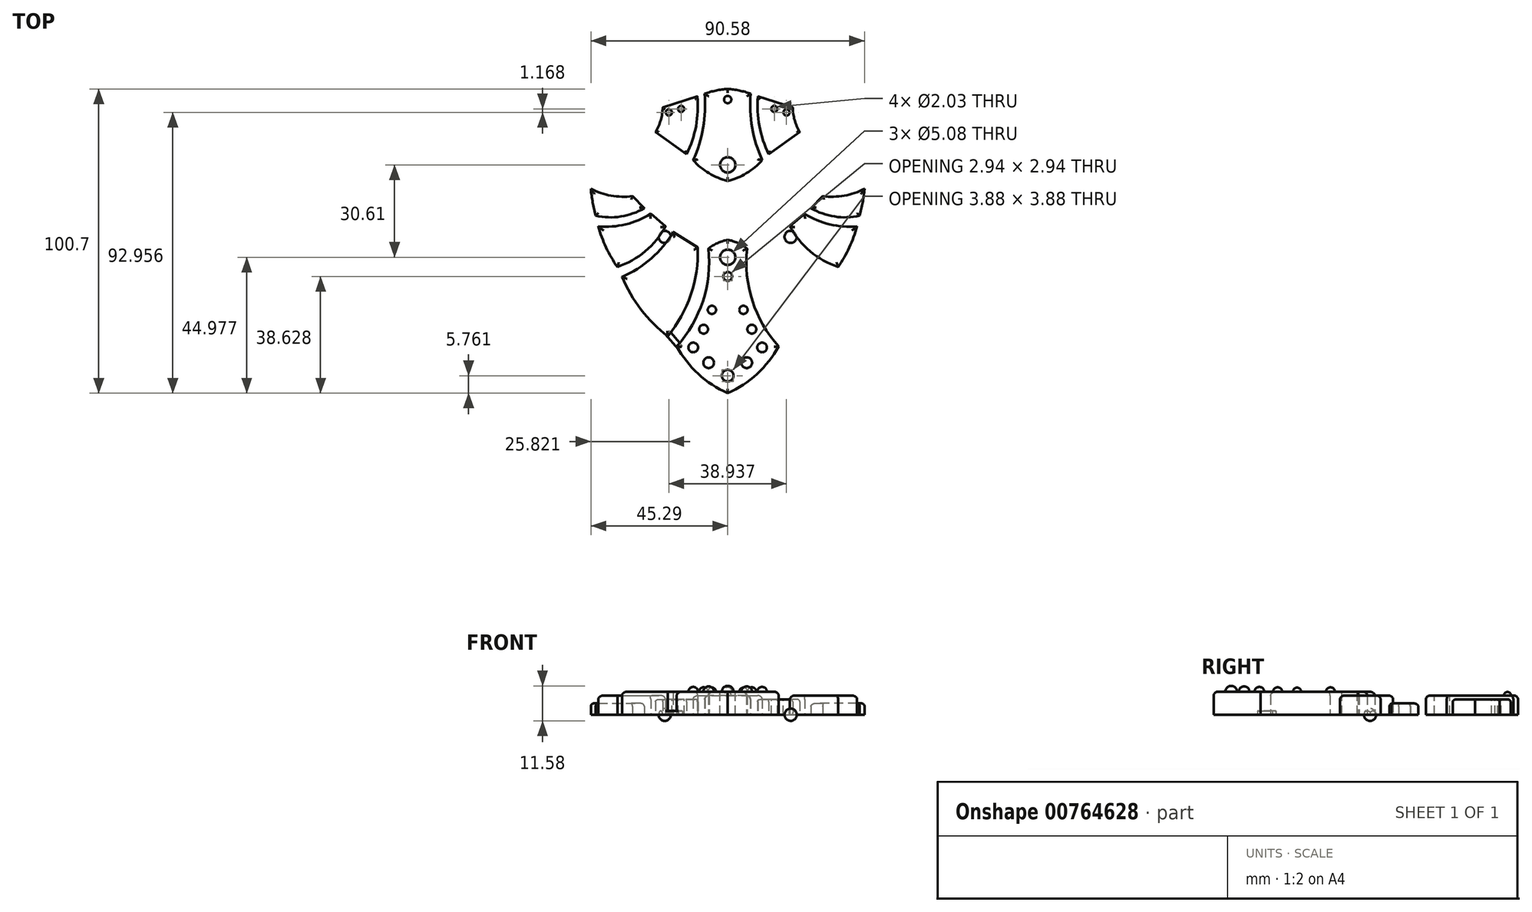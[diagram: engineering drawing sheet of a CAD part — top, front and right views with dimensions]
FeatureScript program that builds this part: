
annotation { "Feature Type Name" : "Feature", "Feature Type Description" : "" }
export const myFeature = defineFeature(function(context is Context, id is Id, definition is map)
    precondition{}
    {
        {
            var Q0;
            Q0=qCreatedBy(makeId("Top.planeOp"),FACE);
            var sketch = newSketch(context, id + "F0", { "sketchPlane" : qUnion([Q0])});
            skArc(sketch, "E0", {"start": v(0, 35.33) * mm, "mid": v(-3.38, 34.2) * mm, "end": v(-6.4, 32.34) * mm});
            skArc(sketch, "E1", {"start": v(-16.87, 0) * mm, "mid": v(-8.18, 15.05) * mm, "end": v(-6.4, 32.34) * mm});
            skArc(sketch, "E2", {"start": v(-16.87, 0) * mm, "mid": v(-9.71, -9.13) * mm, "end": v(0, -15.47) * mm});
            skArc(sketch, "E3.MirrorCS", {"start": v(16.87, 0) * mm, "mid": v(8.18, 15.05) * mm, "end": v(6.4, 32.34) * mm});
            skArc(sketch, "E4.MirrorCS", {"start": v(0, 35.33) * mm, "mid": v(3.38, 34.2) * mm, "end": v(6.4, 32.34) * mm});
            skArc(sketch, "E5.MirrorCS", {"start": v(16.87, 0) * mm, "mid": v(9.71, -9.13) * mm, "end": v(0, -15.47) * mm});
            skSolve(sketch);
        }
        {
            var Q0;
            Q0=makeQuery(id+"F0.imprint","IMPRINT",FACE,{"disambiguationData":[TD([[makeQuery(id+"F0.imprint","IMPRINT",EDGE,{"derivedFrom":sQuery(id+"F0.wireOp",EDGE,"E0")}),1.0]])]});
            extrude(context, id + "F1", {"entities" : qUnion([Q0]), "depth" : 7.62 * mm, "offsetDistance" : 25.4 * mm});
        }
        {
            var Q0;
            Q0=makeQuery(id+"F1.opExtrude","CAP_EDGE",EDGE,{"disambiguationData":[OSD([sQuery(id+"F0.wireOp",EDGE,"E5.MirrorCS")])],"isStart":false});
            var Q1;
            Q1=makeQuery(id+"F1.opExtrude","CAP_FACE",FACE,{"disambiguationData":[OSD([sQuery(id+"F0.wireOp",EDGE,"E0"),sQuery(id+"F0.wireOp",EDGE,"E1"),sQuery(id+"F0.wireOp",EDGE,"E2"),sQuery(id+"F0.wireOp",EDGE,"E3.MirrorCS"),sQuery(id+"F0.wireOp",EDGE,"E4.MirrorCS"),sQuery(id+"F0.wireOp",EDGE,"E5.MirrorCS")])],"isStart":false});
            fillet(context, id + "F2", {"entities" : qUnion([Q0, Q1]), "radius" : 1.27 * mm, "tangentPropagation" : true, "allowEdgeOverflow" : false});
        }
        {
            var Q0;
            Q0=makeQuery(id+"F1.opExtrude","CAP_FACE",FACE,{"disambiguationData":[OSD([sQuery(id+"F0.wireOp",EDGE,"E0"),sQuery(id+"F0.wireOp",EDGE,"E1"),sQuery(id+"F0.wireOp",EDGE,"E2"),sQuery(id+"F0.wireOp",EDGE,"E3.MirrorCS"),sQuery(id+"F0.wireOp",EDGE,"E4.MirrorCS"),sQuery(id+"F0.wireOp",EDGE,"E5.MirrorCS")])],"isStart":false});
            var sketch = newSketch(context, id + "F3", { "sketchPlane" : qUnion([Q0])});
            skCircle(sketch, "E6", {"center": v(0, 29.5) * mm, "radius": 1.8 * mm});
            skSolve(sketch);
        }
        {
            var Q0;
            Q0=sQuery(id+"F3.wireOp",VERTEX,"E6.center");
            var Q1;
            Q1=makeQuery(id+"F1.opExtrude","SWEPT_BODY",BODY,{"disambiguationData":[OSD([sQuery(id+"F0.wireOp",EDGE,"E0"),sQuery(id+"F0.wireOp",EDGE,"E1"),sQuery(id+"F0.wireOp",EDGE,"E2"),sQuery(id+"F0.wireOp",EDGE,"E3.MirrorCS"),sQuery(id+"F0.wireOp",EDGE,"E4.MirrorCS"),sQuery(id+"F0.wireOp",EDGE,"E5.MirrorCS")])]});
            hole(context, id + "F4", {"style" : HoleStyle.SIMPLE, "endStyle" : HoleEndStyle.THROUGH, "holeDiameter" : 5.08 * mm, "majorDiameter" : 6.35 * mm, "isTappedThrough" : true, "tappedDepth" : 12.7 * mm, "tapClearance" : 3, "locations" : qUnion([Q0]), "scope" : qUnion([Q1])});
        }
        {
            var Q0;
            Q0=makeQuery(id+"F1.opExtrude","CAP_FACE",FACE,{"disambiguationData":[OSD([sQuery(id+"F0.wireOp",EDGE,"E0"),sQuery(id+"F0.wireOp",EDGE,"E1"),sQuery(id+"F0.wireOp",EDGE,"E2"),sQuery(id+"F0.wireOp",EDGE,"E3.MirrorCS"),sQuery(id+"F0.wireOp",EDGE,"E4.MirrorCS"),sQuery(id+"F0.wireOp",EDGE,"E5.MirrorCS")])],"isStart":false});
            var sketch = newSketch(context, id + "F5", { "sketchPlane" : qUnion([Q0])});
            skArc(sketch, "E7", {"start": v(0, -11.65) * mm, "mid": v(1.94, -9.7) * mm, "end": v(0, -7.77) * mm});
            skLineSegment(sketch, "E8", {"start": v(0, -7.77) * mm, "end": v(0, -11.65) * mm});
            skSolve(sketch);
        }
        {
            var Q0;
            Q0=makeQuery(id+"F5.imprint","IMPRINT",FACE,{"disambiguationData":[TD([[makeQuery(id+"F5.imprint","IMPRINT",EDGE,{"derivedFrom":sQuery(id+"F5.wireOp",EDGE,"E7")}),1.0]])]});
            var Q1;
            Q1=sQuery(id+"F5.wireOp",EDGE,"E7");
            var Q2;
            Q2=sQuery(id+"F5.wireOp",EDGE,"E8");
            revolve(context, id + "F6", {"operationType" : NewBodyOperationType.ADD, "surfaceOperationType" : NewSurfaceOperationType.ADD, "entities" : qUnion([Q0]), "surfaceEntities" : qUnion([Q1]), "axis" : qUnion([Q2]), "revolveType" : RevolveType.ONE_DIRECTION, "angle" : 180 * degree});
        }
        {
            var Q0;
            Q0=qCreatedBy(makeId("Top.planeOp"),FACE);
            var sketch = newSketch(context, id + "F7", { "sketchPlane" : qUnion([Q0])});
            skArc(sketch, "E9", {"start": v(0, 85.23) * mm, "mid": v(-3.88, 84.74) * mm, "end": v(-7.63, 83.67) * mm});
            skArc(sketch, "E10", {"start": v(-11.43, 61.67) * mm, "mid": v(-8.1, 72.42) * mm, "end": v(-7.63, 83.67) * mm});
            skArc(sketch, "E11", {"start": v(-11.43, 61.67) * mm, "mid": v(-6.23, 57.37) * mm, "end": v(0, 54.75) * mm});
            skArc(sketch, "E12.MirrorCS", {"start": v(11.43, 61.67) * mm, "mid": v(6.23, 57.37) * mm, "end": v(0, 54.75) * mm});
            skArc(sketch, "E13.MirrorCS", {"start": v(0, 85.23) * mm, "mid": v(3.88, 84.74) * mm, "end": v(7.63, 83.67) * mm});
            skArc(sketch, "E14.MirrorCS", {"start": v(11.43, 61.67) * mm, "mid": v(8.1, 72.42) * mm, "end": v(7.63, 83.67) * mm});
            skSolve(sketch);
        }
        {
            var Q0;
            Q0=qSketchRegion(id+"F7",true);
            extrude(context, id + "F8", {"entities" : qUnion([Q0]), "depth" : 6.35 * mm, "offsetDistance" : 25.4 * mm});
        }
        {
            var Q0;
            Q0=makeQuery(id+"F8.opExtrude","CAP_EDGE",EDGE,{"disambiguationData":[OSD([sQuery(id+"F7.wireOp",EDGE,"E14.MirrorCS")])],"isStart":false});
            var Q1;
            Q1=makeQuery(id+"F8.opExtrude","CAP_EDGE",EDGE,{"disambiguationData":[OSD([sQuery(id+"F7.wireOp",EDGE,"E10")])],"isStart":false});
            var Q2;
            Q2=makeQuery(id+"F8.opExtrude","CAP_FACE",FACE,{"disambiguationData":[OSD([sQuery(id+"F7.wireOp",EDGE,"E9"),sQuery(id+"F7.wireOp",EDGE,"E10"),sQuery(id+"F7.wireOp",EDGE,"E11"),sQuery(id+"F7.wireOp",EDGE,"E12.MirrorCS"),sQuery(id+"F7.wireOp",EDGE,"E13.MirrorCS"),sQuery(id+"F7.wireOp",EDGE,"E14.MirrorCS")])],"isStart":false});
            fillet(context, id + "F9", {"entities" : qUnion([Q0, Q1, Q2]), "radius" : 1.27 * mm, "tangentPropagation" : true, "allowEdgeOverflow" : false});
        }
        {
            var Q0;
            Q0=makeQuery(id+"F8.opExtrude","CAP_FACE",FACE,{"disambiguationData":[OSD([sQuery(id+"F7.wireOp",EDGE,"E9"),sQuery(id+"F7.wireOp",EDGE,"E10"),sQuery(id+"F7.wireOp",EDGE,"E11"),sQuery(id+"F7.wireOp",EDGE,"E12.MirrorCS"),sQuery(id+"F7.wireOp",EDGE,"E13.MirrorCS"),sQuery(id+"F7.wireOp",EDGE,"E14.MirrorCS")])],"isStart":false});
            var sketch = newSketch(context, id + "F10", { "sketchPlane" : qUnion([Q0])});
            skCircle(sketch, "E15", {"center": v(0, 60.12) * mm, "radius": 1.7 * mm});
            skSolve(sketch);
        }
        {
            var Q0;
            Q0=sQuery(id+"F10.wireOp",VERTEX,"E15.center");
            var Q1;
            Q1=makeQuery(id+"F8.opExtrude","SWEPT_BODY",BODY,{"disambiguationData":[OSD([sQuery(id+"F7.wireOp",EDGE,"E9"),sQuery(id+"F7.wireOp",EDGE,"E10"),sQuery(id+"F7.wireOp",EDGE,"E11"),sQuery(id+"F7.wireOp",EDGE,"E12.MirrorCS"),sQuery(id+"F7.wireOp",EDGE,"E13.MirrorCS"),sQuery(id+"F7.wireOp",EDGE,"E14.MirrorCS")])]});
            hole(context, id + "F11", {"style" : HoleStyle.SIMPLE, "endStyle" : HoleEndStyle.THROUGH, "holeDiameter" : 5.08 * mm, "majorDiameter" : 6.35 * mm, "isTappedThrough" : true, "tappedDepth" : 12.7 * mm, "tapClearance" : 3, "locations" : qUnion([Q0]), "scope" : qUnion([Q1])});
        }
        {
            var Q0;
            Q0=qCreatedBy(makeId("Top.planeOp"),FACE);
            var sketch = newSketch(context, id + "F12", { "sketchPlane" : qUnion([Q0])});
            skLineSegment(sketch, "E16", {"start": v(-10, 82.76) * mm, "end": v(-21.52, 79.1) * mm});
            skArc(sketch, "E17", {"start": v(-23.89, 70.98) * mm, "mid": v(-22.16, 74.88) * mm, "end": v(-21.52, 79.1) * mm});
            skLineSegment(sketch, "E18", {"start": v(-23.89, 70.98) * mm, "end": v(-13.58, 63.66) * mm});
            skArc(sketch, "E19", {"start": v(-13.58, 63.66) * mm, "mid": v(-10.49, 72.97) * mm, "end": v(-10, 82.76) * mm});
            skSolve(sketch);
        }
        {
            var Q0;
            Q0=makeQuery(id+"F12.imprint","IMPRINT",FACE,{"disambiguationData":[TD([[makeQuery(id+"F12.imprint","IMPRINT",EDGE,{"derivedFrom":sQuery(id+"F12.wireOp",EDGE,"E16")}),1.0]])]});
            extrude(context, id + "F13", {"entities" : qUnion([Q0]), "depth" : 5.08 * mm, "offsetDistance" : 25.4 * mm});
        }
        {
            var Q0;
            Q0=makeQuery(id+"F13.opExtrude","CAP_FACE",FACE,{"disambiguationData":[OSD([sQuery(id+"F12.wireOp",EDGE,"E16"),sQuery(id+"F12.wireOp",EDGE,"E17"),sQuery(id+"F12.wireOp",EDGE,"E18"),sQuery(id+"F12.wireOp",EDGE,"E19")])],"isStart":false});
            fillet(context, id + "F14", {"entities" : qUnion([Q0]), "radius" : 0.76 * mm, "tangentPropagation" : true, "allowEdgeOverflow" : false});
        }
        {
            var Q0;
            Q0=qCreatedBy(makeId("Top.planeOp"),FACE);
            var sketch = newSketch(context, id + "F15", { "sketchPlane" : qUnion([Q0])});
            skLineSegment(sketch, "E20", {"start": v(-9.9, 32.72) * mm, "end": v(-18, 37.86) * mm});
            skArc(sketch, "E21", {"start": v(-34.99, 23.02) * mm, "mid": v(-25.3, 29.08) * mm, "end": v(-18, 37.86) * mm});
            skArc(sketch, "E22", {"start": v(-34.99, 23.02) * mm, "mid": v(-28.71, 12.18) * mm, "end": v(-19.8, 3.37) * mm});
            skArc(sketch, "E23", {"start": v(-19.8, 3.37) * mm, "mid": v(-12.2, 17.15) * mm, "end": v(-9.9, 32.72) * mm});
            skSolve(sketch);
        }
        {
            var Q0;
            Q0=makeQuery(id+"F15.imprint","IMPRINT",FACE,{"disambiguationData":[TD([[makeQuery(id+"F15.imprint","IMPRINT",EDGE,{"derivedFrom":sQuery(id+"F15.wireOp",EDGE,"E20")}),1.0]])]});
            extrude(context, id + "F16", {"entities" : qUnion([Q0]), "depth" : 7.62 * mm, "offsetDistance" : 25.4 * mm});
        }
        {
            var Q0;
            Q0=makeQuery(id+"F16.opExtrude","CAP_FACE",FACE,{"disambiguationData":[OSD([sQuery(id+"F15.wireOp",EDGE,"E20"),sQuery(id+"F15.wireOp",EDGE,"E21"),sQuery(id+"F15.wireOp",EDGE,"E22"),sQuery(id+"F15.wireOp",EDGE,"E23")])],"isStart":false});
            fillet(context, id + "F17", {"entities" : qUnion([Q0]), "radius" : 1.27 * mm, "tangentPropagation" : true, "allowEdgeOverflow" : false});
        }
        {
            var Q0;
            Q0=qCreatedBy(makeId("Top.planeOp"),FACE);
            var sketch = newSketch(context, id + "F18", { "sketchPlane" : qUnion([Q0])});
            skLineSegment(sketch, "E24", {"start": v(-20.6, 39.74) * mm, "end": v(-25.48, 43.9) * mm});
            skArc(sketch, "E25", {"start": v(-36.53, 26.3) * mm, "mid": v(-27.28, 31.5) * mm, "end": v(-20.6, 39.74) * mm});
            skArc(sketch, "E26", {"start": v(-42.83, 39.74) * mm, "mid": v(-40.25, 32.76) * mm, "end": v(-36.53, 26.3) * mm});
            skArc(sketch, "E27", {"start": v(-42.83, 39.74) * mm, "mid": v(-33.81, 40.39) * mm, "end": v(-25.48, 43.9) * mm});
            skSolve(sketch);
        }
        {
            var Q0;
            Q0=makeQuery(id+"F18.imprint","IMPRINT",FACE,{"disambiguationData":[TD([[makeQuery(id+"F18.imprint","IMPRINT",EDGE,{"derivedFrom":sQuery(id+"F18.wireOp",EDGE,"E24")}),1.0]])]});
            extrude(context, id + "F19", {"entities" : qUnion([Q0]), "depth" : 6.35 * mm, "offsetDistance" : 25.4 * mm});
        }
        {
            var Q0;
            Q0=makeQuery(id+"F19.opExtrude","CAP_FACE",FACE,{"disambiguationData":[OSD([sQuery(id+"F18.wireOp",EDGE,"E24"),sQuery(id+"F18.wireOp",EDGE,"E25"),sQuery(id+"F18.wireOp",EDGE,"E26"),sQuery(id+"F18.wireOp",EDGE,"E27")])],"isStart":false});
            fillet(context, id + "F20", {"entities" : qUnion([Q0]), "radius" : 1.27 * mm, "tangentPropagation" : true, "allowEdgeOverflow" : false});
        }
        {
            var Q0;
            Q0=qCreatedBy(makeId("Top.planeOp"),FACE);
            var sketch = newSketch(context, id + "F21", { "sketchPlane" : qUnion([Q0])});
            skLineSegment(sketch, "E28", {"start": v(-27.58, 45.78) * mm, "end": v(-31.53, 49.73) * mm});
            skArc(sketch, "E29", {"start": v(-43.67, 43.28) * mm, "mid": v(-35.38, 43) * mm, "end": v(-27.58, 45.78) * mm});
            skArc(sketch, "E30", {"start": v(-45.3, 52.16) * mm, "mid": v(-44.67, 47.69) * mm, "end": v(-43.67, 43.28) * mm});
            skArc(sketch, "E31", {"start": v(-45.3, 52.16) * mm, "mid": v(-38.6, 49.92) * mm, "end": v(-31.53, 49.73) * mm});
            skSolve(sketch);
        }
        {
            var Q0;
            Q0=makeQuery(id+"F21.imprint","IMPRINT",FACE,{"disambiguationData":[TD([[makeQuery(id+"F21.imprint","IMPRINT",EDGE,{"derivedFrom":sQuery(id+"F21.wireOp",EDGE,"E28")}),1.0]])]});
            extrude(context, id + "F22", {"entities" : qUnion([Q0]), "depth" : 3.8 * mm, "offsetDistance" : 25.4 * mm});
        }
        {
            var Q0;
            Q0=makeQuery(id+"F22.opExtrude","CAP_FACE",FACE,{"disambiguationData":[OSD([sQuery(id+"F21.wireOp",EDGE,"E28"),sQuery(id+"F21.wireOp",EDGE,"E29"),sQuery(id+"F21.wireOp",EDGE,"E30"),sQuery(id+"F21.wireOp",EDGE,"E31")])],"isStart":false});
            fillet(context, id + "F23", {"entities" : qUnion([Q0]), "radius" : 1.02 * mm, "tangentPropagation" : true, "allowEdgeOverflow" : false});
        }
        {
            var Q0;
            Q0=makeQuery(id+"F13.opExtrude","CAP_FACE",FACE,{"disambiguationData":[OSD([sQuery(id+"F12.wireOp",EDGE,"E16"),sQuery(id+"F12.wireOp",EDGE,"E17"),sQuery(id+"F12.wireOp",EDGE,"E18"),sQuery(id+"F12.wireOp",EDGE,"E19")])],"isStart":false});
            var sketch = newSketch(context, id + "F24", { "sketchPlane" : qUnion([Q0])});
            skCircle(sketch, "E32", {"center": v(-19.47, 77.49) * mm, "radius": 1.02 * mm});
            skSolve(sketch);
        }
        {
            var Q0;
            Q0=sQuery(id+"F24.wireOp",VERTEX,"E32.center");
            var Q1;
            Q1=makeQuery(id+"F13.opExtrude","SWEPT_BODY",BODY,{"disambiguationData":[OSD([sQuery(id+"F12.wireOp",EDGE,"E16"),sQuery(id+"F12.wireOp",EDGE,"E17"),sQuery(id+"F12.wireOp",EDGE,"E18"),sQuery(id+"F12.wireOp",EDGE,"E19")])]});
            hole(context, id + "F25", {"style" : HoleStyle.SIMPLE, "endStyle" : HoleEndStyle.THROUGH, "holeDiameter" : 2.03 * mm, "majorDiameter" : 6.35 * mm, "isTappedThrough" : true, "tappedDepth" : 12.7 * mm, "tapClearance" : 3, "locations" : qUnion([Q0]), "scope" : qUnion([Q1])});
        }
        {
            var Q0;
            Q0=makeQuery(id+"F13.opExtrude","CAP_FACE",FACE,{"disambiguationData":[OSD([sQuery(id+"F12.wireOp",EDGE,"E16"),sQuery(id+"F12.wireOp",EDGE,"E17"),sQuery(id+"F12.wireOp",EDGE,"E18"),sQuery(id+"F12.wireOp",EDGE,"E19")])],"isStart":false});
            var sketch = newSketch(context, id + "F26", { "sketchPlane" : qUnion([Q0])});
            skCircle(sketch, "E33", {"center": v(-15.42, 78.65) * mm, "radius": 1.01 * mm});
            skSolve(sketch);
        }
        {
            var Q0;
            Q0=sQuery(id+"F26.wireOp",VERTEX,"E33.center");
            var Q1;
            Q1=makeQuery(id+"F13.opExtrude","SWEPT_BODY",BODY,{"disambiguationData":[OSD([sQuery(id+"F12.wireOp",EDGE,"E16"),sQuery(id+"F12.wireOp",EDGE,"E17"),sQuery(id+"F12.wireOp",EDGE,"E18"),sQuery(id+"F12.wireOp",EDGE,"E19")])]});
            hole(context, id + "F27", {"style" : HoleStyle.SIMPLE, "endStyle" : HoleEndStyle.THROUGH, "holeDiameter" : 2.03 * mm, "majorDiameter" : 6.35 * mm, "isTappedThrough" : true, "tappedDepth" : 12.7 * mm, "tapClearance" : 3, "locations" : qUnion([Q0]), "scope" : qUnion([Q1])});
        }
        {
            var Q0;
            Q0=makeQuery(id+"F8.opExtrude","CAP_FACE",FACE,{"disambiguationData":[OSD([sQuery(id+"F7.wireOp",EDGE,"E9"),sQuery(id+"F7.wireOp",EDGE,"E10"),sQuery(id+"F7.wireOp",EDGE,"E11"),sQuery(id+"F7.wireOp",EDGE,"E12.MirrorCS"),sQuery(id+"F7.wireOp",EDGE,"E13.MirrorCS"),sQuery(id+"F7.wireOp",EDGE,"E14.MirrorCS")])],"isStart":false});
            var sketch = newSketch(context, id + "F28", { "sketchPlane" : qUnion([Q0])});
            skArc(sketch, "E34", {"start": v(0, 82.96) * mm, "mid": v(-1.21, 81.75) * mm, "end": v(0, 80.54) * mm});
            skLineSegment(sketch, "E35", {"start": v(0, 82.96) * mm, "end": v(0, 80.54) * mm});
            skSolve(sketch);
        }
        {
            var Q0;
            Q0=makeQuery(id+"F28.imprint","IMPRINT",FACE,{"disambiguationData":[TD([[makeQuery(id+"F28.imprint","IMPRINT",EDGE,{"derivedFrom":sQuery(id+"F28.wireOp",EDGE,"E34")}),1.0]])]});
            var Q1;
            Q1=sQuery(id+"F28.wireOp",EDGE,"E34");
            var Q2;
            Q2=sQuery(id+"F28.wireOp",EDGE,"E35");
            revolve(context, id + "F29", {"operationType" : NewBodyOperationType.ADD, "surfaceOperationType" : NewSurfaceOperationType.NEW, "entities" : qUnion([Q0]), "surfaceEntities" : qUnion([Q1]), "axis" : qUnion([Q2]), "revolveType" : RevolveType.FULL});
        }
        {
            var Q0;
            Q0=makeQuery(id+"F1.opExtrude","CAP_FACE",FACE,{"disambiguationData":[OSD([sQuery(id+"F0.wireOp",EDGE,"E0"),sQuery(id+"F0.wireOp",EDGE,"E1"),sQuery(id+"F0.wireOp",EDGE,"E2"),sQuery(id+"F0.wireOp",EDGE,"E3.MirrorCS"),sQuery(id+"F0.wireOp",EDGE,"E4.MirrorCS"),sQuery(id+"F0.wireOp",EDGE,"E5.MirrorCS")])],"isStart":false});
            var sketch = newSketch(context, id + "F30", { "sketchPlane" : qUnion([Q0])});
            skArc(sketch, "E36", {"start": v(-11.39, 1.23) * mm, "mid": v(-12.98, -0.37) * mm, "end": v(-11.39, -1.97) * mm});
            skLineSegment(sketch, "E37", {"start": v(-11.39, 1.23) * mm, "end": v(-11.39, -1.97) * mm});
            skSolve(sketch);
        }
        {
            var Q0;
            Q0=makeQuery(id+"F30.imprint","IMPRINT",FACE,{"disambiguationData":[TD([[makeQuery(id+"F30.imprint","IMPRINT",EDGE,{"derivedFrom":sQuery(id+"F30.wireOp",EDGE,"E36")}),1.0]])]});
            var Q1;
            Q1=sQuery(id+"F30.wireOp",EDGE,"E36");
            var Q2;
            Q2=sQuery(id+"F30.wireOp",EDGE,"E37");
            revolve(context, id + "F31", {"operationType" : NewBodyOperationType.ADD, "surfaceOperationType" : NewSurfaceOperationType.ADD, "entities" : qUnion([Q0]), "surfaceEntities" : qUnion([Q1]), "axis" : qUnion([Q2]), "revolveType" : RevolveType.FULL});
        }
        {
            var Q0;
            Q0=qCreatedBy(makeId("Top.planeOp"),FACE);
            var sketch = newSketch(context, id + "F32", { "sketchPlane" : qUnion([Q0])});
            skArc(sketch, "E38", {"start": v(-8.2, 27.38) * mm, "mid": v(-5.99, 29.58) * mm, "end": v(-8.2, 31.79) * mm});
            skLineSegment(sketch, "E39", {"start": v(-8.2, 27.38) * mm, "end": v(-8.2, 31.79) * mm});
            skSolve(sketch);
        }
        {
            var Q0;
            Q0=sQuery(id+"F32.wireOp",EDGE,"E38");
            var Q1;
            Q1=sQuery(id+"F32.wireOp",EDGE,"E39");
            revolve(context, id + "F33", {"bodyType" : ToolBodyType.SURFACE, "surfaceOperationType" : NewSurfaceOperationType.NEW, "surfaceEntities" : qUnion([Q0]), "axis" : qUnion([Q1]), "revolveType" : RevolveType.FULL});
        }
        {
            var Q0;
            Q0=qCreatedBy(makeId("Top.planeOp"),FACE);
            var sketch = newSketch(context, id + "F34", { "sketchPlane" : qUnion([Q0])});
            skArc(sketch, "E40", {"start": v(-20.84, 34.25) * mm, "mid": v(-18.82, 36.27) * mm, "end": v(-20.84, 38.3) * mm});
            skLineSegment(sketch, "E41", {"start": v(-20.84, 34.25) * mm, "end": v(-20.84, 38.3) * mm});
            skSolve(sketch);
        }
        {
            var Q0;
            Q0=qSketchRegion(id+"F34",true);
            var Q1;
            Q1=sQuery(id+"F34.wireOp",EDGE,"E41");
            revolve(context, id + "F35", {"surfaceOperationType" : NewSurfaceOperationType.NEW, "entities" : qUnion([Q0]), "axis" : qUnion([Q1]), "revolveType" : RevolveType.FULL});
        }
        {
            var Q0;
            Q0=qCreatedBy(makeId("Top.planeOp"),FACE);
            var sketch = newSketch(context, id + "F36", { "sketchPlane" : qUnion([Q0])});
            skArc(sketch, "E42", {"start": v(-29.07, 41.32) * mm, "mid": v(-27.22, 43.18) * mm, "end": v(-29.07, 45.03) * mm});
            skLineSegment(sketch, "E43", {"start": v(-29.07, 41.32) * mm, "end": v(-29.07, 45.03) * mm});
            skSolve(sketch);
        }
        {
            var Q0;
            Q0=sQuery(id+"F36.wireOp",EDGE,"E42");
            var Q1;
            Q1=sQuery(id+"F36.wireOp",EDGE,"E43");
            revolve(context, id + "F37", {"bodyType" : ToolBodyType.SURFACE, "surfaceOperationType" : NewSurfaceOperationType.NEW, "surfaceEntities" : qUnion([Q0]), "axis" : qUnion([Q1]), "revolveType" : RevolveType.FULL});
        }
        {
            var Q0;
            Q0=makeQuery(id+"F1.opExtrude","CAP_FACE",FACE,{"disambiguationData":[OSD([sQuery(id+"F0.wireOp",EDGE,"E0"),sQuery(id+"F0.wireOp",EDGE,"E1"),sQuery(id+"F0.wireOp",EDGE,"E2"),sQuery(id+"F0.wireOp",EDGE,"E3.MirrorCS"),sQuery(id+"F0.wireOp",EDGE,"E4.MirrorCS"),sQuery(id+"F0.wireOp",EDGE,"E5.MirrorCS")])],"isStart":false});
            var sketch = newSketch(context, id + "F38", { "sketchPlane" : qUnion([Q0])});
            skArc(sketch, "E44", {"start": v(-6.3, -7.2) * mm, "mid": v(-4.53, -5.42) * mm, "end": v(-6.3, -3.65) * mm});
            skLineSegment(sketch, "E45", {"start": v(-6.3, -3.65) * mm, "end": v(-6.3, -7.2) * mm});
            skSolve(sketch);
        }
        {
            var Q0;
            Q0=makeQuery(id+"F38.imprint","IMPRINT",FACE,{"disambiguationData":[TD([[makeQuery(id+"F38.imprint","IMPRINT",EDGE,{"derivedFrom":sQuery(id+"F38.wireOp",EDGE,"E44")}),1.0]])]});
            var Q1;
            Q1=sQuery(id+"F38.wireOp",EDGE,"E44");
            var Q2;
            Q2=sQuery(id+"F38.wireOp",EDGE,"E45");
            revolve(context, id + "F39", {"operationType" : NewBodyOperationType.ADD, "surfaceOperationType" : NewSurfaceOperationType.NEW, "entities" : qUnion([Q0]), "surfaceEntities" : qUnion([Q1]), "axis" : qUnion([Q2]), "revolveType" : RevolveType.FULL});
        }
        {
            var Q0;
            Q0=makeQuery(id+"F1.opExtrude","CAP_FACE",FACE,{"disambiguationData":[OSD([sQuery(id+"F0.wireOp",EDGE,"E0"),sQuery(id+"F0.wireOp",EDGE,"E1"),sQuery(id+"F0.wireOp",EDGE,"E2"),sQuery(id+"F0.wireOp",EDGE,"E3.MirrorCS"),sQuery(id+"F0.wireOp",EDGE,"E4.MirrorCS"),sQuery(id+"F0.wireOp",EDGE,"E5.MirrorCS")])],"isStart":false});
            var sketch = newSketch(context, id + "F40", { "sketchPlane" : qUnion([Q0])});
            skArc(sketch, "E46", {"start": v(-7.98, 4.2) * mm, "mid": v(-6.5, 5.68) * mm, "end": v(-7.98, 7.16) * mm});
            skLineSegment(sketch, "E47", {"start": v(-7.98, 7.16) * mm, "end": v(-7.98, 4.2) * mm});
            skSolve(sketch);
        }
        {
            var Q0;
            Q0=makeQuery(id+"F40.imprint","IMPRINT",FACE,{"disambiguationData":[TD([[makeQuery(id+"F40.imprint","IMPRINT",EDGE,{"derivedFrom":sQuery(id+"F40.wireOp",EDGE,"E46")}),1.0]])]});
            var Q1;
            Q1=sQuery(id+"F40.wireOp",EDGE,"E46");
            var Q2;
            Q2=sQuery(id+"F40.wireOp",EDGE,"E47");
            revolve(context, id + "F41", {"operationType" : NewBodyOperationType.ADD, "surfaceOperationType" : NewSurfaceOperationType.NEW, "entities" : qUnion([Q0]), "surfaceEntities" : qUnion([Q1]), "axis" : qUnion([Q2]), "revolveType" : RevolveType.FULL});
        }
        {
            var Q0;
            Q0=qCreatedBy(makeId("Top.planeOp"),FACE);
            var sketch = newSketch(context, id + "F42", { "sketchPlane" : qUnion([Q0])});
            skLineSegment(sketch, "E48", {"start": v(-20.58, 3.98) * mm, "end": v(-16.29, -0.95) * mm});
            skLineSegment(sketch, "E49", {"start": v(-16.29, -0.95) * mm, "end": v(-15.04, 0.14) * mm});
            skLineSegment(sketch, "E50", {"start": v(-15.04, 0.14) * mm, "end": v(-19.4, 5.14) * mm});
            skLineSegment(sketch, "E51", {"start": v(-19.4, 5.14) * mm, "end": v(-20.58, 3.98) * mm});
            skSolve(sketch);
        }
        {
            var Q0;
            Q0=makeQuery(id+"F42.imprint","IMPRINT",FACE,{"disambiguationData":[TD([[makeQuery(id+"F42.imprint","IMPRINT",EDGE,{"derivedFrom":sQuery(id+"F42.wireOp",EDGE,"E48")}),1.0]])]});
            extrude(context, id + "F43", {"entities" : qUnion([Q0]), "depth" : 1.27 * mm, "offsetDistance" : 25.4 * mm});
        }
        {
            var Q0;
            Q0=makeQuery(id+"F1.opExtrude","CAP_FACE",FACE,{"disambiguationData":[OSD([sQuery(id+"F0.wireOp",EDGE,"E0"),sQuery(id+"F0.wireOp",EDGE,"E1"),sQuery(id+"F0.wireOp",EDGE,"E2"),sQuery(id+"F0.wireOp",EDGE,"E3.MirrorCS"),sQuery(id+"F0.wireOp",EDGE,"E4.MirrorCS"),sQuery(id+"F0.wireOp",EDGE,"E5.MirrorCS")])],"isStart":false});
            var sketch = newSketch(context, id + "F44", { "sketchPlane" : qUnion([Q0])});
            skArc(sketch, "E52", {"start": v(-5.22, 10.73) * mm, "mid": v(-3.85, 12.1) * mm, "end": v(-5.22, 13.46) * mm});
            skLineSegment(sketch, "E53", {"start": v(-5.22, 13.46) * mm, "end": v(-5.22, 10.73) * mm});
            skSolve(sketch);
        }
        {
            var Q0;
            Q0=makeQuery(id+"F44.imprint","IMPRINT",FACE,{"disambiguationData":[TD([[makeQuery(id+"F44.imprint","IMPRINT",EDGE,{"derivedFrom":sQuery(id+"F44.wireOp",EDGE,"E52")}),1.0]])]});
            var Q1;
            Q1=sQuery(id+"F44.wireOp",EDGE,"E52");
            var Q2;
            Q2=sQuery(id+"F44.wireOp",EDGE,"E53");
            revolve(context, id + "F45", {"operationType" : NewBodyOperationType.ADD, "surfaceOperationType" : NewSurfaceOperationType.NEW, "entities" : qUnion([Q0]), "surfaceEntities" : qUnion([Q1]), "axis" : qUnion([Q2]), "revolveType" : RevolveType.FULL});
        }
        {
            var Q0;
            Q0=makeQuery(id+"F1.opExtrude","CAP_FACE",FACE,{"disambiguationData":[OSD([sQuery(id+"F0.wireOp",EDGE,"E0"),sQuery(id+"F0.wireOp",EDGE,"E1"),sQuery(id+"F0.wireOp",EDGE,"E2"),sQuery(id+"F0.wireOp",EDGE,"E3.MirrorCS"),sQuery(id+"F0.wireOp",EDGE,"E4.MirrorCS"),sQuery(id+"F0.wireOp",EDGE,"E5.MirrorCS")])],"isStart":false});
            var sketch = newSketch(context, id + "F46", { "sketchPlane" : qUnion([Q0])});
            skArc(sketch, "E54", {"start": v(-3.58, 17.36) * mm, "mid": v(-2.32, 18.63) * mm, "end": v(-3.58, 19.9) * mm});
            skLineSegment(sketch, "E55", {"start": v(-3.58, 19.9) * mm, "end": v(-3.58, 17.36) * mm});
            skSolve(sketch);
        }
        {
            var Q0;
            Q0=sQuery(id+"F46.wireOp",EDGE,"E54");
            var Q1;
            Q1=sQuery(id+"F46.wireOp",EDGE,"E55");
            revolve(context, id + "F47", {"bodyType" : ToolBodyType.SURFACE, "surfaceOperationType" : NewSurfaceOperationType.NEW, "surfaceEntities" : qUnion([Q0]), "axis" : qUnion([Q1]), "revolveType" : RevolveType.FULL});
        }
        {
            var Q0;
            Q0=makeQuery(id+"F47.opRevolve","SWEPT_BODY",BODY,{"disambiguationData":[OSD([sQuery(id+"F46.wireOp",EDGE,"E54")])]});
            var Q1;
            Q1=qCreatedBy(makeId("Right.planeOp"),FACE);
            mirror(context, id + "F48", {"entities" : qUnion([Q0]), "mirrorPlane" : qUnion([Q1])});
        }
        {
            var Q0;
            Q0=makeQuery(id+"F1.opExtrude","CAP_FACE",FACE,{"disambiguationData":[OSD([sQuery(id+"F0.wireOp",EDGE,"E0"),sQuery(id+"F0.wireOp",EDGE,"E1"),sQuery(id+"F0.wireOp",EDGE,"E2"),sQuery(id+"F0.wireOp",EDGE,"E3.MirrorCS"),sQuery(id+"F0.wireOp",EDGE,"E4.MirrorCS"),sQuery(id+"F0.wireOp",EDGE,"E5.MirrorCS")])],"isStart":false});
            var sketch = newSketch(context, id + "F49", { "sketchPlane" : qUnion([Q0])});
            skArc(sketch, "E56", {"start": v(0, 21.69) * mm, "mid": v(1.47, 23.16) * mm, "end": v(0, 24.63) * mm});
            skLineSegment(sketch, "E57", {"start": v(0, 24.63) * mm, "end": v(0, 21.69) * mm});
            skSolve(sketch);
        }
        {
            var Q0;
            Q0=makeQuery(id+"F49.imprint","IMPRINT",FACE,{"disambiguationData":[TD([[makeQuery(id+"F49.imprint","IMPRINT",EDGE,{"derivedFrom":sQuery(id+"F49.wireOp",EDGE,"E56")}),1.0]])]});
            var Q1;
            Q1=sQuery(id+"F49.wireOp",EDGE,"E56");
            var Q2;
            Q2=sQuery(id+"F49.wireOp",EDGE,"E57");
            revolve(context, id + "F50", {"operationType" : NewBodyOperationType.ADD, "surfaceOperationType" : NewSurfaceOperationType.NEW, "entities" : qUnion([Q0]), "surfaceEntities" : qUnion([Q1]), "axis" : qUnion([Q2]), "revolveType" : RevolveType.FULL});
        }
        {
            var Q0;
            Q0=makeQuery(id+"F8.opExtrude","CAP_FACE",FACE,{"disambiguationData":[OSD([sQuery(id+"F7.wireOp",EDGE,"E9"),sQuery(id+"F7.wireOp",EDGE,"E10"),sQuery(id+"F7.wireOp",EDGE,"E11"),sQuery(id+"F7.wireOp",EDGE,"E12.MirrorCS"),sQuery(id+"F7.wireOp",EDGE,"E13.MirrorCS"),sQuery(id+"F7.wireOp",EDGE,"E14.MirrorCS")])],"isStart":false});
            var sketch = newSketch(context, id + "F51", { "sketchPlane" : qUnion([Q0])});
            skArc(sketch, "E58", {"start": v(-4.05, 80.13) * mm, "mid": v(-2.9, 81.3) * mm, "end": v(-4.05, 82.46) * mm});
            skLineSegment(sketch, "E59", {"start": v(-4.05, 82.46) * mm, "end": v(-4.05, 80.13) * mm});
            skSolve(sketch);
        }
        {
            var Q0;
            Q0=sQuery(id+"F51.wireOp",EDGE,"E58");
            var Q1;
            Q1=sQuery(id+"F51.wireOp",EDGE,"E59");
            revolve(context, id + "F52", {"bodyType" : ToolBodyType.SURFACE, "surfaceOperationType" : NewSurfaceOperationType.NEW, "surfaceEntities" : qUnion([Q0]), "axis" : qUnion([Q1]), "revolveType" : RevolveType.FULL});
        }
        {
            var Q0;
            Q0=makeQuery(id+"F52.opRevolve","SWEPT_BODY",BODY,{"disambiguationData":[OSD([sQuery(id+"F51.wireOp",EDGE,"E58")])]});
            var Q1;
            Q1=qCreatedBy(makeId("Right.planeOp"),FACE);
            mirror(context, id + "F53", {"entities" : qUnion([Q0]), "mirrorPlane" : qUnion([Q1])});
        }
        {
            var Q0;
            Q0=makeQuery(id+"F8.opExtrude","CAP_FACE",FACE,{"disambiguationData":[OSD([sQuery(id+"F7.wireOp",EDGE,"E9"),sQuery(id+"F7.wireOp",EDGE,"E10"),sQuery(id+"F7.wireOp",EDGE,"E11"),sQuery(id+"F7.wireOp",EDGE,"E12.MirrorCS"),sQuery(id+"F7.wireOp",EDGE,"E13.MirrorCS"),sQuery(id+"F7.wireOp",EDGE,"E14.MirrorCS")])],"isStart":false});
            var sketch = newSketch(context, id + "F54", { "sketchPlane" : qUnion([Q0])});
            skArc(sketch, "E60", {"start": v(-6.03, 60.77) * mm, "mid": v(-4.09, 62.72) * mm, "end": v(-6.03, 64.67) * mm});
            skLineSegment(sketch, "E61", {"start": v(-6.03, 64.67) * mm, "end": v(-6.03, 60.77) * mm});
            skSolve(sketch);
        }
        {
            var Q0;
            Q0=sQuery(id+"F54.wireOp",EDGE,"E60");
            var Q1;
            Q1=sQuery(id+"F54.wireOp",EDGE,"E61");
            revolve(context, id + "F55", {"bodyType" : ToolBodyType.SURFACE, "surfaceOperationType" : NewSurfaceOperationType.NEW, "surfaceEntities" : qUnion([Q0]), "axis" : qUnion([Q1]), "revolveType" : RevolveType.FULL});
        }
        {
            var Q0;
            Q0=makeQuery(id+"F55.opRevolve","SWEPT_BODY",BODY,{"disambiguationData":[OSD([sQuery(id+"F54.wireOp",EDGE,"E60")])]});
            var Q1;
            Q1=qCreatedBy(makeId("Right.planeOp"),FACE);
            mirror(context, id + "F56", {"entities" : qUnion([Q0]), "mirrorPlane" : qUnion([Q1])});
        }
        {
            var Q0;
            Q0=qCreatedBy(makeId("Top.planeOp"),FACE);
            var sketch = newSketch(context, id + "F57", { "sketchPlane" : qUnion([Q0])});
            skArc(sketch, "E62", {"start": v(-8.7, 78.7) * mm, "mid": v(-7.1, 80.3) * mm, "end": v(-8.7, 81.93) * mm});
            skLineSegment(sketch, "E63", {"start": v(-8.7, 78.7) * mm, "end": v(-8.7, 81.93) * mm});
            skSolve(sketch);
        }
        {
            var Q0;
            Q0=sQuery(id+"F57.wireOp",EDGE,"E62");
            var Q1;
            Q1=sQuery(id+"F57.wireOp",EDGE,"E63");
            revolve(context, id + "F58", {"bodyType" : ToolBodyType.SURFACE, "surfaceOperationType" : NewSurfaceOperationType.NEW, "surfaceEntities" : qUnion([Q0]), "axis" : qUnion([Q1]), "revolveType" : RevolveType.FULL});
        }
        {
            var Q0;
            Q0=makeQuery(id+"F16.opExtrude","CAP_FACE",FACE,{"disambiguationData":[OSD([sQuery(id+"F15.wireOp",EDGE,"E20"),sQuery(id+"F15.wireOp",EDGE,"E21"),sQuery(id+"F15.wireOp",EDGE,"E22"),sQuery(id+"F15.wireOp",EDGE,"E23")])],"isStart":false});
            var sketch = newSketch(context, id + "F59", { "sketchPlane" : qUnion([Q0])});
            skArc(sketch, "E64", {"start": v(-20.59, 8.42) * mm, "mid": v(-19.03, 9.98) * mm, "end": v(-20.59, 11.54) * mm});
            skLineSegment(sketch, "E65", {"start": v(-20.59, 11.54) * mm, "end": v(-20.59, 8.42) * mm});
            skSolve(sketch);
        }
        {
            var Q0;
            Q0=sQuery(id+"F59.wireOp",EDGE,"E64");
            var Q1;
            Q1=sQuery(id+"F59.wireOp",EDGE,"E65");
            revolve(context, id + "F60", {"bodyType" : ToolBodyType.SURFACE, "surfaceOperationType" : NewSurfaceOperationType.NEW, "surfaceEntities" : qUnion([Q0]), "axis" : qUnion([Q1]), "revolveType" : RevolveType.FULL});
        }
        {
            var Q0;
            Q0=makeQuery(id+"F16.opExtrude","CAP_FACE",FACE,{"disambiguationData":[OSD([sQuery(id+"F15.wireOp",EDGE,"E20"),sQuery(id+"F15.wireOp",EDGE,"E21"),sQuery(id+"F15.wireOp",EDGE,"E22"),sQuery(id+"F15.wireOp",EDGE,"E23")])],"isStart":false});
            var sketch = newSketch(context, id + "F61", { "sketchPlane" : qUnion([Q0])});
            skArc(sketch, "E66", {"start": v(-17.5, 13.56) * mm, "mid": v(-16.15, 14.91) * mm, "end": v(-17.5, 16.26) * mm});
            skLineSegment(sketch, "E67", {"start": v(-17.5, 16.26) * mm, "end": v(-17.5, 13.56) * mm});
            skSolve(sketch);
        }
        {
            var Q0;
            Q0=sQuery(id+"F61.wireOp",EDGE,"E66");
            var Q1;
            Q1=sQuery(id+"F61.wireOp",EDGE,"E67");
            revolve(context, id + "F62", {"bodyType" : ToolBodyType.SURFACE, "surfaceOperationType" : NewSurfaceOperationType.NEW, "surfaceEntities" : qUnion([Q0]), "axis" : qUnion([Q1]), "revolveType" : RevolveType.FULL});
        }
        {
            var Q0;
            Q0=makeQuery(id+"F16.opExtrude","CAP_FACE",FACE,{"disambiguationData":[OSD([sQuery(id+"F15.wireOp",EDGE,"E20"),sQuery(id+"F15.wireOp",EDGE,"E21"),sQuery(id+"F15.wireOp",EDGE,"E22"),sQuery(id+"F15.wireOp",EDGE,"E23")])],"isStart":false});
            var sketch = newSketch(context, id + "F63", { "sketchPlane" : qUnion([Q0])});
            skArc(sketch, "E68", {"start": v(-15.25, 18.99) * mm, "mid": v(-14.01, 20.22) * mm, "end": v(-15.25, 21.45) * mm});
            skLineSegment(sketch, "E69", {"start": v(-15.25, 21.45) * mm, "end": v(-15.25, 18.99) * mm});
            skSolve(sketch);
        }
        {
            var Q0;
            Q0=sQuery(id+"F63.wireOp",EDGE,"E68");
            var Q1;
            Q1=sQuery(id+"F63.wireOp",EDGE,"E69");
            revolve(context, id + "F64", {"bodyType" : ToolBodyType.SURFACE, "surfaceOperationType" : NewSurfaceOperationType.NEW, "surfaceEntities" : qUnion([Q0]), "axis" : qUnion([Q1]), "revolveType" : RevolveType.FULL});
        }
        {
            var Q0;
            Q0=makeQuery(id+"F8.opExtrude","CAP_FACE",FACE,{"disambiguationData":[OSD([sQuery(id+"F7.wireOp",EDGE,"E9"),sQuery(id+"F7.wireOp",EDGE,"E10"),sQuery(id+"F7.wireOp",EDGE,"E11"),sQuery(id+"F7.wireOp",EDGE,"E12.MirrorCS"),sQuery(id+"F7.wireOp",EDGE,"E13.MirrorCS"),sQuery(id+"F7.wireOp",EDGE,"E14.MirrorCS")])],"isStart":false});
            var sketch = newSketch(context, id + "F65", { "sketchPlane" : qUnion([Q0])});
            skArc(sketch, "E70", {"start": v(-4.84, 67.63) * mm, "mid": v(-3.42, 69.05) * mm, "end": v(-4.84, 70.48) * mm});
            skLineSegment(sketch, "E71", {"start": v(-4.84, 70.48) * mm, "end": v(-4.84, 67.63) * mm});
            skSolve(sketch);
        }
        {
            var Q0;
            Q0=sQuery(id+"F65.wireOp",EDGE,"E70");
            var Q1;
            Q1=sQuery(id+"F65.wireOp",EDGE,"E71");
            revolve(context, id + "F66", {"bodyType" : ToolBodyType.SURFACE, "surfaceOperationType" : NewSurfaceOperationType.NEW, "surfaceEntities" : qUnion([Q0]), "axis" : qUnion([Q1]), "revolveType" : RevolveType.FULL});
        }
        {
            var Q0;
            Q0=makeQuery(id+"F66.opRevolve","SWEPT_BODY",BODY,{"disambiguationData":[OSD([sQuery(id+"F65.wireOp",EDGE,"E70")])]});
            var Q1;
            Q1=qCreatedBy(makeId("Right.planeOp"),FACE);
            mirror(context, id + "F67", {"entities" : qUnion([Q0]), "mirrorPlane" : qUnion([Q1])});
        }
        {
            var Q0;
            Q0=makeQuery(id+"F8.opExtrude","CAP_FACE",FACE,{"disambiguationData":[OSD([sQuery(id+"F7.wireOp",EDGE,"E9"),sQuery(id+"F7.wireOp",EDGE,"E10"),sQuery(id+"F7.wireOp",EDGE,"E11"),sQuery(id+"F7.wireOp",EDGE,"E12.MirrorCS"),sQuery(id+"F7.wireOp",EDGE,"E13.MirrorCS"),sQuery(id+"F7.wireOp",EDGE,"E14.MirrorCS")])],"isStart":false});
            var sketch = newSketch(context, id + "F68", { "sketchPlane" : qUnion([Q0])});
            skArc(sketch, "E72", {"start": v(-4.33, 74.27) * mm, "mid": v(-3.3, 75.3) * mm, "end": v(-4.33, 76.32) * mm});
            skLineSegment(sketch, "E73", {"start": v(-4.33, 76.32) * mm, "end": v(-4.33, 74.27) * mm});
            skSolve(sketch);
        }
        {
            var Q0;
            Q0=sQuery(id+"F68.wireOp",EDGE,"E72");
            var Q1;
            Q1=sQuery(id+"F68.wireOp",EDGE,"E73");
            revolve(context, id + "F69", {"bodyType" : ToolBodyType.SURFACE, "surfaceOperationType" : NewSurfaceOperationType.NEW, "surfaceEntities" : qUnion([Q0]), "axis" : qUnion([Q1]), "revolveType" : RevolveType.FULL});
        }
        {
            var Q0;
            Q0=makeQuery(id+"F69.opRevolve","SWEPT_BODY",BODY,{"disambiguationData":[OSD([sQuery(id+"F68.wireOp",EDGE,"E72")])]});
            var Q1;
            Q1=qCreatedBy(makeId("Right.planeOp"),FACE);
            mirror(context, id + "F70", {"entities" : qUnion([Q0]), "mirrorPlane" : qUnion([Q1])});
        }
        {
            var Q0;
            Q0=makeQuery(id+"F13.opExtrude","CAP_FACE",FACE,{"disambiguationData":[OSD([sQuery(id+"F12.wireOp",EDGE,"E16"),sQuery(id+"F12.wireOp",EDGE,"E17"),sQuery(id+"F12.wireOp",EDGE,"E18"),sQuery(id+"F12.wireOp",EDGE,"E19")])],"isStart":false});
            var sketch = newSketch(context, id + "F71", { "sketchPlane" : qUnion([Q0])});
            skArc(sketch, "E74", {"start": v(-12.23, 78.79) * mm, "mid": v(-11.46, 79.56) * mm, "end": v(-12.23, 80.34) * mm});
            skLineSegment(sketch, "E75", {"start": v(-12.23, 80.34) * mm, "end": v(-12.23, 78.79) * mm});
            skSolve(sketch);
        }
        {
            var Q0;
            Q0=sQuery(id+"F71.wireOp",EDGE,"E74");
            var Q1;
            Q1=sQuery(id+"F71.wireOp",EDGE,"E75");
            revolve(context, id + "F72", {"bodyType" : ToolBodyType.SURFACE, "surfaceOperationType" : NewSurfaceOperationType.NEW, "surfaceEntities" : qUnion([Q0]), "axis" : qUnion([Q1]), "revolveType" : RevolveType.FULL});
        }
        {
            var Q0;
            Q0=makeQuery(id+"F16.opExtrude","CAP_FACE",FACE,{"disambiguationData":[OSD([sQuery(id+"F15.wireOp",EDGE,"E20"),sQuery(id+"F15.wireOp",EDGE,"E21"),sQuery(id+"F15.wireOp",EDGE,"E22"),sQuery(id+"F15.wireOp",EDGE,"E23")])],"isStart":false});
            var sketch = newSketch(context, id + "F73", { "sketchPlane" : qUnion([Q0])});
            skArc(sketch, "E76", {"start": v(-13.25, 29.54) * mm, "mid": v(-12.11, 30.67) * mm, "end": v(-13.25, 31.8) * mm});
            skLineSegment(sketch, "E77", {"start": v(-13.25, 31.8) * mm, "end": v(-13.25, 29.54) * mm});
            skSolve(sketch);
        }
        {
            var Q0;
            Q0=sQuery(id+"F73.wireOp",EDGE,"E76");
            var Q1;
            Q1=sQuery(id+"F73.wireOp",EDGE,"E77");
            revolve(context, id + "F74", {"bodyType" : ToolBodyType.SURFACE, "surfaceOperationType" : NewSurfaceOperationType.NEW, "surfaceEntities" : qUnion([Q0]), "axis" : qUnion([Q1]), "revolveType" : RevolveType.FULL});
        }
        {
            var Q0;
            Q0=makeQuery(id+"F16.opExtrude","CAP_FACE",FACE,{"disambiguationData":[OSD([sQuery(id+"F15.wireOp",EDGE,"E20"),sQuery(id+"F15.wireOp",EDGE,"E21"),sQuery(id+"F15.wireOp",EDGE,"E22"),sQuery(id+"F15.wireOp",EDGE,"E23")])],"isStart":false});
            var sketch = newSketch(context, id + "F75", { "sketchPlane" : qUnion([Q0])});
            skArc(sketch, "E78", {"start": v(-14.01, 24.36) * mm, "mid": v(-12.82, 25.56) * mm, "end": v(-14.01, 26.76) * mm});
            skLineSegment(sketch, "E79", {"start": v(-14.01, 26.76) * mm, "end": v(-14.01, 24.36) * mm});
            skSolve(sketch);
        }
        {
            var Q0;
            Q0=sQuery(id+"F75.wireOp",EDGE,"E78");
            var Q1;
            Q1=sQuery(id+"F75.wireOp",EDGE,"E79");
            revolve(context, id + "F76", {"bodyType" : ToolBodyType.SURFACE, "surfaceOperationType" : NewSurfaceOperationType.NEW, "surfaceEntities" : qUnion([Q0]), "axis" : qUnion([Q1]), "revolveType" : RevolveType.FULL});
        }
        {
            var Q0;
            Q0=makeQuery(id+"F16.opExtrude","CAP_FACE",FACE,{"disambiguationData":[OSD([sQuery(id+"F15.wireOp",EDGE,"E20"),sQuery(id+"F15.wireOp",EDGE,"E21"),sQuery(id+"F15.wireOp",EDGE,"E22"),sQuery(id+"F15.wireOp",EDGE,"E23")])],"isStart":false});
            var sketch = newSketch(context, id + "F77", { "sketchPlane" : qUnion([Q0])});
            skArc(sketch, "E80", {"start": v(-17, 32.1) * mm, "mid": v(-15.88, 33.2) * mm, "end": v(-17, 34.32) * mm});
            skLineSegment(sketch, "E81", {"start": v(-17, 34.32) * mm, "end": v(-17, 32.1) * mm});
            skSolve(sketch);
        }
        {
            var Q0;
            Q0=sQuery(id+"F77.wireOp",EDGE,"E80");
            var Q1;
            Q1=sQuery(id+"F77.wireOp",EDGE,"E81");
            revolve(context, id + "F78", {"bodyType" : ToolBodyType.SURFACE, "surfaceOperationType" : NewSurfaceOperationType.NEW, "surfaceEntities" : qUnion([Q0]), "axis" : qUnion([Q1]), "revolveType" : RevolveType.FULL});
        }
        {
            var Q0;
            Q0=makeQuery(id+"F16.opExtrude","CAP_FACE",FACE,{"disambiguationData":[OSD([sQuery(id+"F15.wireOp",EDGE,"E20"),sQuery(id+"F15.wireOp",EDGE,"E21"),sQuery(id+"F15.wireOp",EDGE,"E22"),sQuery(id+"F15.wireOp",EDGE,"E23")])],"isStart":false});
            var sketch = newSketch(context, id + "F79", { "sketchPlane" : qUnion([Q0])});
            skArc(sketch, "E82", {"start": v(-29.56, 19.4) * mm, "mid": v(-28.01, 20.95) * mm, "end": v(-29.56, 22.5) * mm});
            skLineSegment(sketch, "E83", {"start": v(-29.56, 22.5) * mm, "end": v(-29.56, 19.4) * mm});
            skSolve(sketch);
        }
        {
            var Q0;
            Q0=sQuery(id+"F79.wireOp",EDGE,"E82");
            var Q1;
            Q1=sQuery(id+"F79.wireOp",EDGE,"E83");
            revolve(context, id + "F80", {"bodyType" : ToolBodyType.SURFACE, "surfaceOperationType" : NewSurfaceOperationType.NEW, "surfaceEntities" : qUnion([Q0]), "axis" : qUnion([Q1]), "revolveType" : RevolveType.FULL});
        }
        {
            var Q0;
            Q0=makeQuery(id+"F16.opExtrude","CAP_FACE",FACE,{"disambiguationData":[OSD([sQuery(id+"F15.wireOp",EDGE,"E20"),sQuery(id+"F15.wireOp",EDGE,"E21"),sQuery(id+"F15.wireOp",EDGE,"E22"),sQuery(id+"F15.wireOp",EDGE,"E23")])],"isStart":false});
            var sketch = newSketch(context, id + "F81", { "sketchPlane" : qUnion([Q0])});
            skArc(sketch, "E84", {"start": v(-25.53, 13.51) * mm, "mid": v(-23.94, 15.1) * mm, "end": v(-25.53, 16.7) * mm});
            skLineSegment(sketch, "E85", {"start": v(-25.53, 16.7) * mm, "end": v(-25.53, 13.51) * mm});
            skSolve(sketch);
        }
        {
            var Q0;
            Q0=sQuery(id+"F81.wireOp",EDGE,"E84");
            var Q1;
            Q1=sQuery(id+"F81.wireOp",EDGE,"E85");
            revolve(context, id + "F82", {"bodyType" : ToolBodyType.SURFACE, "surfaceOperationType" : NewSurfaceOperationType.NEW, "surfaceEntities" : qUnion([Q0]), "axis" : qUnion([Q1]), "revolveType" : RevolveType.FULL});
        }
        {
            var Q0;
            Q0=makeQuery(id+"F16.opExtrude","CAP_FACE",FACE,{"disambiguationData":[OSD([sQuery(id+"F15.wireOp",EDGE,"E20"),sQuery(id+"F15.wireOp",EDGE,"E21"),sQuery(id+"F15.wireOp",EDGE,"E22"),sQuery(id+"F15.wireOp",EDGE,"E23")])],"isStart":false});
            var sketch = newSketch(context, id + "F83", { "sketchPlane" : qUnion([Q0])});
            skArc(sketch, "E86", {"start": v(-24.4, 23.64) * mm, "mid": v(-23.06, 24.98) * mm, "end": v(-24.4, 26.32) * mm});
            skLineSegment(sketch, "E87", {"start": v(-24.4, 26.32) * mm, "end": v(-24.4, 23.64) * mm});
            skSolve(sketch);
        }
        {
            var Q0;
            Q0=sQuery(id+"F83.wireOp",EDGE,"E86");
            var Q1;
            Q1=sQuery(id+"F83.wireOp",EDGE,"E87");
            revolve(context, id + "F84", {"bodyType" : ToolBodyType.SURFACE, "surfaceOperationType" : NewSurfaceOperationType.NEW, "surfaceEntities" : qUnion([Q0]), "axis" : qUnion([Q1]), "revolveType" : RevolveType.FULL});
        }
        {
            var Q0;
            Q0=makeQuery(id+"F16.opExtrude","CAP_FACE",FACE,{"disambiguationData":[OSD([sQuery(id+"F15.wireOp",EDGE,"E20"),sQuery(id+"F15.wireOp",EDGE,"E21"),sQuery(id+"F15.wireOp",EDGE,"E22"),sQuery(id+"F15.wireOp",EDGE,"E23")])],"isStart":false});
            var sketch = newSketch(context, id + "F85", { "sketchPlane" : qUnion([Q0])});
            skArc(sketch, "E88", {"start": v(-20.27, 27.83) * mm, "mid": v(-19.08, 29.02) * mm, "end": v(-20.27, 30.21) * mm});
            skLineSegment(sketch, "E89", {"start": v(-20.27, 30.21) * mm, "end": v(-20.27, 27.83) * mm});
            skSolve(sketch);
        }
        {
            var Q0;
            Q0=sQuery(id+"F85.wireOp",EDGE,"E88");
            var Q1;
            Q1=sQuery(id+"F85.wireOp",EDGE,"E89");
            revolve(context, id + "F86", {"bodyType" : ToolBodyType.SURFACE, "surfaceOperationType" : NewSurfaceOperationType.NEW, "surfaceEntities" : qUnion([Q0]), "axis" : qUnion([Q1]), "revolveType" : RevolveType.FULL});
        }
        {
            var Q0;
            Q0=makeQuery(id+"F19.opExtrude","CAP_FACE",FACE,{"disambiguationData":[OSD([sQuery(id+"F18.wireOp",EDGE,"E24"),sQuery(id+"F18.wireOp",EDGE,"E25"),sQuery(id+"F18.wireOp",EDGE,"E26"),sQuery(id+"F18.wireOp",EDGE,"E27")])],"isStart":false});
            var sketch = newSketch(context, id + "F87", { "sketchPlane" : qUnion([Q0])});
            skArc(sketch, "E90", {"start": v(-35.16, 29.3) * mm, "mid": v(-33.93, 30.53) * mm, "end": v(-35.16, 31.76) * mm});
            skLineSegment(sketch, "E91", {"start": v(-35.16, 31.76) * mm, "end": v(-35.16, 29.3) * mm});
            skSolve(sketch);
        }
        {
            var Q0;
            Q0=sQuery(id+"F87.wireOp",EDGE,"E90");
            var Q1;
            Q1=sQuery(id+"F87.wireOp",EDGE,"E91");
            revolve(context, id + "F88", {"bodyType" : ToolBodyType.SURFACE, "surfaceOperationType" : NewSurfaceOperationType.NEW, "surfaceEntities" : qUnion([Q0]), "axis" : qUnion([Q1]), "revolveType" : RevolveType.FULL});
        }
        {
            var Q0;
            Q0=makeQuery(id+"F19.opExtrude","CAP_FACE",FACE,{"disambiguationData":[OSD([sQuery(id+"F18.wireOp",EDGE,"E24"),sQuery(id+"F18.wireOp",EDGE,"E25"),sQuery(id+"F18.wireOp",EDGE,"E26"),sQuery(id+"F18.wireOp",EDGE,"E27")])],"isStart":false});
            var sketch = newSketch(context, id + "F89", { "sketchPlane" : qUnion([Q0])});
            skArc(sketch, "E92", {"start": v(-38.1, 35.18) * mm, "mid": v(-36.88, 36.39) * mm, "end": v(-38.1, 37.6) * mm});
            skLineSegment(sketch, "E93", {"start": v(-38.1, 37.6) * mm, "end": v(-38.1, 35.18) * mm});
            skSolve(sketch);
        }
        {
            var Q0;
            Q0=sQuery(id+"F89.wireOp",EDGE,"E92");
            var Q1;
            Q1=sQuery(id+"F89.wireOp",EDGE,"E93");
            revolve(context, id + "F90", {"bodyType" : ToolBodyType.SURFACE, "surfaceOperationType" : NewSurfaceOperationType.NEW, "surfaceEntities" : qUnion([Q0]), "axis" : qUnion([Q1]), "revolveType" : RevolveType.FULL});
        }
        {
            var Q0;
            Q0=makeQuery(id+"F22.opExtrude","CAP_FACE",FACE,{"disambiguationData":[OSD([sQuery(id+"F21.wireOp",EDGE,"E28"),sQuery(id+"F21.wireOp",EDGE,"E29"),sQuery(id+"F21.wireOp",EDGE,"E30"),sQuery(id+"F21.wireOp",EDGE,"E31")])],"isStart":false});
            var sketch = newSketch(context, id + "F91", { "sketchPlane" : qUnion([Q0])});
            skArc(sketch, "E94", {"start": v(-41.12, 45.34) * mm, "mid": v(-39.76, 46.7) * mm, "end": v(-41.12, 48.07) * mm});
            skLineSegment(sketch, "E95", {"start": v(-41.12, 48.07) * mm, "end": v(-41.12, 45.34) * mm});
            skSolve(sketch);
        }
        {
            var Q0;
            Q0=sQuery(id+"F91.wireOp",EDGE,"E94");
            var Q1;
            Q1=sQuery(id+"F91.wireOp",EDGE,"E95");
            revolve(context, id + "F92", {"bodyType" : ToolBodyType.SURFACE, "surfaceOperationType" : NewSurfaceOperationType.NEW, "surfaceEntities" : qUnion([Q0]), "axis" : qUnion([Q1]), "revolveType" : RevolveType.FULL});
        }
        {
            var Q0;
            Q0=makeQuery(id+"F22.opExtrude","CAP_FACE",FACE,{"disambiguationData":[OSD([sQuery(id+"F21.wireOp",EDGE,"E28"),sQuery(id+"F21.wireOp",EDGE,"E29"),sQuery(id+"F21.wireOp",EDGE,"E30"),sQuery(id+"F21.wireOp",EDGE,"E31")])],"isStart":false});
            var sketch = newSketch(context, id + "F93", { "sketchPlane" : qUnion([Q0])});
            skArc(sketch, "E96", {"start": v(-36.9, 45.08) * mm, "mid": v(-35.77, 46.2) * mm, "end": v(-36.9, 47.32) * mm});
            skLineSegment(sketch, "E97", {"start": v(-36.9, 47.32) * mm, "end": v(-36.9, 45.08) * mm});
            skSolve(sketch);
        }
        {
            var Q0;
            Q0=sQuery(id+"F93.wireOp",EDGE,"E96");
            var Q1;
            Q1=sQuery(id+"F93.wireOp",EDGE,"E97");
            revolve(context, id + "F94", {"bodyType" : ToolBodyType.SURFACE, "surfaceOperationType" : NewSurfaceOperationType.NEW, "surfaceEntities" : qUnion([Q0]), "axis" : qUnion([Q1]), "revolveType" : RevolveType.FULL});
        }
        {
            var Q0;
            Q0=makeQuery(id+"F22.opExtrude","CAP_FACE",FACE,{"disambiguationData":[OSD([sQuery(id+"F21.wireOp",EDGE,"E28"),sQuery(id+"F21.wireOp",EDGE,"E29"),sQuery(id+"F21.wireOp",EDGE,"E30"),sQuery(id+"F21.wireOp",EDGE,"E31")])],"isStart":false});
            var sketch = newSketch(context, id + "F95", { "sketchPlane" : qUnion([Q0])});
            skArc(sketch, "E98", {"start": v(-32.99, 45.72) * mm, "mid": v(-32.07, 46.64) * mm, "end": v(-32.99, 47.55) * mm});
            skLineSegment(sketch, "E99", {"start": v(-32.99, 47.55) * mm, "end": v(-32.99, 45.72) * mm});
            skSolve(sketch);
        }
        {
            var Q0;
            Q0=sQuery(id+"F95.wireOp",EDGE,"E98");
            var Q1;
            Q1=sQuery(id+"F95.wireOp",EDGE,"E99");
            revolve(context, id + "F96", {"bodyType" : ToolBodyType.SURFACE, "surfaceOperationType" : NewSurfaceOperationType.NEW, "surfaceEntities" : qUnion([Q0]), "axis" : qUnion([Q1]), "revolveType" : RevolveType.FULL});
        }
        {
            var Q0;
            Q0=makeQuery(id+"F19.opExtrude","CAP_FACE",FACE,{"disambiguationData":[OSD([sQuery(id+"F18.wireOp",EDGE,"E24"),sQuery(id+"F18.wireOp",EDGE,"E25"),sQuery(id+"F18.wireOp",EDGE,"E26"),sQuery(id+"F18.wireOp",EDGE,"E27")])],"isStart":false});
            var sketch = newSketch(context, id + "F97", { "sketchPlane" : qUnion([Q0])});
            skArc(sketch, "E100", {"start": v(-25.52, 38.34) * mm, "mid": v(-24.36, 39.5) * mm, "end": v(-25.52, 40.65) * mm});
            skLineSegment(sketch, "E101", {"start": v(-25.52, 40.65) * mm, "end": v(-25.52, 38.34) * mm});
            skSolve(sketch);
        }
        {
            var Q0;
            Q0=sQuery(id+"F97.wireOp",EDGE,"E100");
            var Q1;
            Q1=sQuery(id+"F97.wireOp",EDGE,"E101");
            revolve(context, id + "F98", {"bodyType" : ToolBodyType.SURFACE, "surfaceOperationType" : NewSurfaceOperationType.NEW, "surfaceEntities" : qUnion([Q0]), "axis" : qUnion([Q1]), "revolveType" : RevolveType.FULL});
        }
        {
            var Q0;
            Q0=makeQuery(id+"F19.opExtrude","CAP_FACE",FACE,{"disambiguationData":[OSD([sQuery(id+"F18.wireOp",EDGE,"E24"),sQuery(id+"F18.wireOp",EDGE,"E25"),sQuery(id+"F18.wireOp",EDGE,"E26"),sQuery(id+"F18.wireOp",EDGE,"E27")])],"isStart":false});
            var sketch = newSketch(context, id + "F99", { "sketchPlane" : qUnion([Q0])});
            skArc(sketch, "E102", {"start": v(-28.87, 35.92) * mm, "mid": v(-27.9, 36.89) * mm, "end": v(-28.87, 37.86) * mm});
            skLineSegment(sketch, "E103", {"start": v(-28.87, 37.86) * mm, "end": v(-28.87, 35.92) * mm});
            skSolve(sketch);
        }
        {
            var Q0;
            Q0=sQuery(id+"F99.wireOp",EDGE,"E102");
            var Q1;
            Q1=sQuery(id+"F99.wireOp",EDGE,"E103");
            revolve(context, id + "F100", {"bodyType" : ToolBodyType.SURFACE, "surfaceOperationType" : NewSurfaceOperationType.NEW, "surfaceEntities" : qUnion([Q0]), "axis" : qUnion([Q1]), "revolveType" : RevolveType.FULL});
        }
        {
            var Q0;
            Q0=makeQuery(id+"F19.opExtrude","CAP_FACE",FACE,{"disambiguationData":[OSD([sQuery(id+"F18.wireOp",EDGE,"E24"),sQuery(id+"F18.wireOp",EDGE,"E25"),sQuery(id+"F18.wireOp",EDGE,"E26"),sQuery(id+"F18.wireOp",EDGE,"E27")])],"isStart":false});
            var sketch = newSketch(context, id + "F101", { "sketchPlane" : qUnion([Q0])});
            skArc(sketch, "E104", {"start": v(-33.27, 33.03) * mm, "mid": v(-31.47, 34.83) * mm, "end": v(-33.27, 36.63) * mm});
            skLineSegment(sketch, "E105", {"start": v(-33.27, 36.63) * mm, "end": v(-33.27, 33.03) * mm});
            skSolve(sketch);
        }
        {
            var Q0;
            Q0=sQuery(id+"F101.wireOp",EDGE,"E104");
            var Q1;
            Q1=sQuery(id+"F101.wireOp",EDGE,"E105");
            revolve(context, id + "F102", {"bodyType" : ToolBodyType.SURFACE, "surfaceOperationType" : NewSurfaceOperationType.NEW, "surfaceEntities" : qUnion([Q0]), "axis" : qUnion([Q1]), "revolveType" : RevolveType.FULL});
        }
        {
            var Q0;
            Q0=makeQuery(id+"F13.opExtrude","CAP_FACE",FACE,{"disambiguationData":[OSD([sQuery(id+"F12.wireOp",EDGE,"E16"),sQuery(id+"F12.wireOp",EDGE,"E17"),sQuery(id+"F12.wireOp",EDGE,"E18"),sQuery(id+"F12.wireOp",EDGE,"E19")])],"isStart":false});
            var sketch = newSketch(context, id + "F103", { "sketchPlane" : qUnion([Q0])});
            skArc(sketch, "E106", {"start": v(-14.87, 67.2) * mm, "mid": v(-13.62, 68.44) * mm, "end": v(-14.87, 69.68) * mm});
            skLineSegment(sketch, "E107", {"start": v(-14.87, 69.68) * mm, "end": v(-14.87, 67.2) * mm});
            skSolve(sketch);
        }
        {
            var Q0;
            Q0=sQuery(id+"F103.wireOp",EDGE,"E106");
            var Q1;
            Q1=sQuery(id+"F103.wireOp",EDGE,"E107");
            revolve(context, id + "F104", {"bodyType" : ToolBodyType.SURFACE, "surfaceOperationType" : NewSurfaceOperationType.NEW, "surfaceEntities" : qUnion([Q0]), "axis" : qUnion([Q1]), "revolveType" : RevolveType.FULL});
        }
        {
            var Q0;
            Q0=makeQuery(id+"F13.opExtrude","CAP_FACE",FACE,{"disambiguationData":[OSD([sQuery(id+"F12.wireOp",EDGE,"E16"),sQuery(id+"F12.wireOp",EDGE,"E17"),sQuery(id+"F12.wireOp",EDGE,"E18"),sQuery(id+"F12.wireOp",EDGE,"E19")])],"isStart":false});
            var sketch = newSketch(context, id + "F105", { "sketchPlane" : qUnion([Q0])});
            skArc(sketch, "E108", {"start": v(-20.31, 70.93) * mm, "mid": v(-19.14, 72.1) * mm, "end": v(-20.31, 73.28) * mm});
            skLineSegment(sketch, "E109", {"start": v(-20.31, 73.28) * mm, "end": v(-20.31, 70.93) * mm});
            skSolve(sketch);
        }
        {
            var Q0;
            Q0=sQuery(id+"F105.wireOp",EDGE,"E108");
            var Q1;
            Q1=sQuery(id+"F105.wireOp",EDGE,"E109");
            revolve(context, id + "F106", {"bodyType" : ToolBodyType.SURFACE, "surfaceOperationType" : NewSurfaceOperationType.NEW, "surfaceEntities" : qUnion([Q0]), "axis" : qUnion([Q1]), "revolveType" : RevolveType.FULL});
        }
        {
            var Q0;
            Q0=makeQuery(id+"F13.opExtrude","CAP_FACE",FACE,{"disambiguationData":[OSD([sQuery(id+"F12.wireOp",EDGE,"E16"),sQuery(id+"F12.wireOp",EDGE,"E17"),sQuery(id+"F12.wireOp",EDGE,"E18"),sQuery(id+"F12.wireOp",EDGE,"E19")])],"isStart":false});
            var sketch = newSketch(context, id + "F107", { "sketchPlane" : qUnion([Q0])});
            skArc(sketch, "E110", {"start": v(-17.65, 69.39) * mm, "mid": v(-16.74, 70.3) * mm, "end": v(-17.65, 71.2) * mm});
            skLineSegment(sketch, "E111", {"start": v(-17.65, 71.2) * mm, "end": v(-17.65, 69.39) * mm});
            skSolve(sketch);
        }
        {
            var Q0;
            Q0=sQuery(id+"F107.wireOp",EDGE,"E110");
            var Q1;
            Q1=sQuery(id+"F107.wireOp",EDGE,"E111");
            revolve(context, id + "F108", {"bodyType" : ToolBodyType.SURFACE, "surfaceOperationType" : NewSurfaceOperationType.NEW, "surfaceEntities" : qUnion([Q0]), "axis" : qUnion([Q1]), "revolveType" : RevolveType.FULL});
        }
        {
            var Q0;
            Q0=makeQuery(id+"F13.opExtrude","CAP_FACE",FACE,{"disambiguationData":[OSD([sQuery(id+"F12.wireOp",EDGE,"E16"),sQuery(id+"F12.wireOp",EDGE,"E17"),sQuery(id+"F12.wireOp",EDGE,"E18"),sQuery(id+"F12.wireOp",EDGE,"E19")])],"isStart":false});
            var sketch = newSketch(context, id + "F109", { "sketchPlane" : qUnion([Q0])});
            skArc(sketch, "E112", {"start": v(-13.34, 71.68) * mm, "mid": v(-12.28, 72.75) * mm, "end": v(-13.34, 73.8) * mm});
            skLineSegment(sketch, "E113", {"start": v(-13.34, 73.8) * mm, "end": v(-13.34, 71.68) * mm});
            skSolve(sketch);
        }
        {
            var Q0;
            Q0=sQuery(id+"F109.wireOp",EDGE,"E112");
            var Q1;
            Q1=sQuery(id+"F109.wireOp",EDGE,"E113");
            revolve(context, id + "F110", {"bodyType" : ToolBodyType.SURFACE, "surfaceOperationType" : NewSurfaceOperationType.NEW, "surfaceEntities" : qUnion([Q0]), "axis" : qUnion([Q1]), "revolveType" : RevolveType.FULL});
        }
        {
            var Q0;
            Q0=makeQuery(id+"F13.opExtrude","CAP_FACE",FACE,{"disambiguationData":[OSD([sQuery(id+"F12.wireOp",EDGE,"E16"),sQuery(id+"F12.wireOp",EDGE,"E17"),sQuery(id+"F12.wireOp",EDGE,"E18"),sQuery(id+"F12.wireOp",EDGE,"E19")])],"isStart":false});
            var sketch = newSketch(context, id + "F111", { "sketchPlane" : qUnion([Q0])});
            skArc(sketch, "E114", {"start": v(-12.57, 75.48) * mm, "mid": v(-11.73, 76.32) * mm, "end": v(-12.57, 77.15) * mm});
            skLineSegment(sketch, "E115", {"start": v(-12.57, 77.15) * mm, "end": v(-12.57, 75.48) * mm});
            skSolve(sketch);
        }
        {
            var Q0;
            Q0=sQuery(id+"F111.wireOp",EDGE,"E114");
            var Q1;
            Q1=sQuery(id+"F111.wireOp",EDGE,"E115");
            revolve(context, id + "F112", {"bodyType" : ToolBodyType.SURFACE, "surfaceOperationType" : NewSurfaceOperationType.NEW, "surfaceEntities" : qUnion([Q0]), "axis" : qUnion([Q1]), "revolveType" : RevolveType.FULL});
        }
        {
            var Q0;
            Q0=makeQuery(id+"F13.opExtrude","SWEPT_BODY",BODY,{"disambiguationData":[OSD([sQuery(id+"F12.wireOp",EDGE,"E16"),sQuery(id+"F12.wireOp",EDGE,"E17"),sQuery(id+"F12.wireOp",EDGE,"E18"),sQuery(id+"F12.wireOp",EDGE,"E19")])]});
            var Q1;
            Q1=makeQuery(id+"F72.opRevolve","SWEPT_BODY",BODY,{"disambiguationData":[OSD([sQuery(id+"F71.wireOp",EDGE,"E74")])]});
            var Q2;
            Q2=makeQuery(id+"F104.opRevolve","SWEPT_BODY",BODY,{"disambiguationData":[OSD([sQuery(id+"F103.wireOp",EDGE,"E106")])]});
            var Q3;
            Q3=makeQuery(id+"F106.opRevolve","SWEPT_BODY",BODY,{"disambiguationData":[OSD([sQuery(id+"F105.wireOp",EDGE,"E108")])]});
            var Q4;
            Q4=makeQuery(id+"F108.opRevolve","SWEPT_BODY",BODY,{"disambiguationData":[OSD([sQuery(id+"F107.wireOp",EDGE,"E110")])]});
            var Q5;
            Q5=makeQuery(id+"F110.opRevolve","SWEPT_BODY",BODY,{"disambiguationData":[OSD([sQuery(id+"F109.wireOp",EDGE,"E112")])]});
            var Q6;
            Q6=makeQuery(id+"F112.opRevolve","SWEPT_BODY",BODY,{"disambiguationData":[OSD([sQuery(id+"F111.wireOp",EDGE,"E114")])]});
            var Q7;
            Q7=qCreatedBy(makeId("Right.planeOp"),FACE);
            mirror(context, id + "F113", {"entities" : qUnion([Q0, Q1, Q2, Q3, Q4, Q5, Q6]), "mirrorPlane" : qUnion([Q7])});
        }
        {
            var Q0;
            Q0=makeQuery(id+"F22.opExtrude","SWEPT_BODY",BODY,{"disambiguationData":[OSD([sQuery(id+"F21.wireOp",EDGE,"E28"),sQuery(id+"F21.wireOp",EDGE,"E29"),sQuery(id+"F21.wireOp",EDGE,"E30"),sQuery(id+"F21.wireOp",EDGE,"E31")])]});
            var Q1;
            Q1=makeQuery(id+"F92.opRevolve","SWEPT_BODY",BODY,{"disambiguationData":[OSD([sQuery(id+"F91.wireOp",EDGE,"E94")])]});
            var Q2;
            Q2=makeQuery(id+"F94.opRevolve","SWEPT_BODY",BODY,{"disambiguationData":[OSD([sQuery(id+"F93.wireOp",EDGE,"E96")])]});
            var Q3;
            Q3=makeQuery(id+"F96.opRevolve","SWEPT_BODY",BODY,{"disambiguationData":[OSD([sQuery(id+"F95.wireOp",EDGE,"E98")])]});
            var Q4;
            Q4=qCreatedBy(makeId("Right.planeOp"),FACE);
            mirror(context, id + "F114", {"entities" : qUnion([Q0, Q1, Q2, Q3]), "mirrorPlane" : qUnion([Q4])});
        }
        {
            var Q0;
            Q0=makeQuery(id+"F19.opExtrude","SWEPT_BODY",BODY,{"disambiguationData":[OSD([sQuery(id+"F18.wireOp",EDGE,"E24"),sQuery(id+"F18.wireOp",EDGE,"E25"),sQuery(id+"F18.wireOp",EDGE,"E26"),sQuery(id+"F18.wireOp",EDGE,"E27")])]});
            var Q1;
            Q1=makeQuery(id+"F88.opRevolve","SWEPT_BODY",BODY,{"disambiguationData":[OSD([sQuery(id+"F87.wireOp",EDGE,"E90")])]});
            var Q2;
            Q2=makeQuery(id+"F90.opRevolve","SWEPT_BODY",BODY,{"disambiguationData":[OSD([sQuery(id+"F89.wireOp",EDGE,"E92")])]});
            var Q3;
            Q3=makeQuery(id+"F98.opRevolve","SWEPT_BODY",BODY,{"disambiguationData":[OSD([sQuery(id+"F97.wireOp",EDGE,"E100")])]});
            var Q4;
            Q4=makeQuery(id+"F100.opRevolve","SWEPT_BODY",BODY,{"disambiguationData":[OSD([sQuery(id+"F99.wireOp",EDGE,"E102")])]});
            var Q5;
            Q5=makeQuery(id+"F102.opRevolve","SWEPT_BODY",BODY,{"disambiguationData":[OSD([sQuery(id+"F101.wireOp",EDGE,"E104")])]});
            var Q6;
            Q6=makeQuery(id+"F22.opExtrude","SWEPT_BODY",BODY,{"disambiguationData":[OSD([sQuery(id+"F21.wireOp",EDGE,"E28"),sQuery(id+"F21.wireOp",EDGE,"E29"),sQuery(id+"F21.wireOp",EDGE,"E30"),sQuery(id+"F21.wireOp",EDGE,"E31")])]});
            var Q7;
            Q7=qCreatedBy(makeId("Right.planeOp"),FACE);
            mirror(context, id + "F115", {"operationType" : NewBodyOperationType.ADD, "entities" : qUnion([Q0, Q1, Q2, Q3, Q4, Q5, Q6]), "mirrorPlane" : qUnion([Q7])});
        }
        {
            var Q0;
            Q0=makeQuery(id+"F37.opRevolve","SWEPT_BODY",BODY,{"disambiguationData":[OSD([sQuery(id+"F36.wireOp",EDGE,"E42")])]});
            var Q1;
            Q1=qCreatedBy(makeId("Right.planeOp"),FACE);
            mirror(context, id + "F116", {"entities" : qUnion([Q0]), "mirrorPlane" : qUnion([Q1])});
        }
        {
            var Q0;
            Q0=makeQuery(id+"F35.opRevolve","SWEPT_BODY",BODY,{"disambiguationData":[OSD([sQuery(id+"F34.wireOp",EDGE,"E40"),sQuery(id+"F34.wireOp",EDGE,"E41")])]});
            var Q1;
            Q1=qCreatedBy(makeId("Right.planeOp"),FACE);
            mirror(context, id + "F117", {"operationType" : NewBodyOperationType.ADD, "entities" : qUnion([Q0]), "mirrorPlane" : qUnion([Q1])});
        }
        {
            var Q0;
            Q0=makeQuery(id+"F1.opExtrude","SWEPT_BODY",BODY,{"disambiguationData":[OSD([sQuery(id+"F0.wireOp",EDGE,"E0"),sQuery(id+"F0.wireOp",EDGE,"E1"),sQuery(id+"F0.wireOp",EDGE,"E2"),sQuery(id+"F0.wireOp",EDGE,"E3.MirrorCS"),sQuery(id+"F0.wireOp",EDGE,"E4.MirrorCS"),sQuery(id+"F0.wireOp",EDGE,"E5.MirrorCS")])]});
            var Q1;
            Q1=makeQuery(id+"F62.opRevolve","SWEPT_BODY",BODY,{"disambiguationData":[OSD([sQuery(id+"F61.wireOp",EDGE,"E66")])]});
            var Q2;
            Q2=makeQuery(id+"F64.opRevolve","SWEPT_BODY",BODY,{"disambiguationData":[OSD([sQuery(id+"F63.wireOp",EDGE,"E68")])]});
            var Q3;
            Q3=makeQuery(id+"F74.opRevolve","SWEPT_BODY",BODY,{"disambiguationData":[OSD([sQuery(id+"F73.wireOp",EDGE,"E76")])]});
            var Q4;
            Q4=makeQuery(id+"F76.opRevolve","SWEPT_BODY",BODY,{"disambiguationData":[OSD([sQuery(id+"F75.wireOp",EDGE,"E78")])]});
            var Q5;
            Q5=makeQuery(id+"F78.opRevolve","SWEPT_BODY",BODY,{"disambiguationData":[OSD([sQuery(id+"F77.wireOp",EDGE,"E80")])]});
            var Q6;
            Q6=makeQuery(id+"F19.opExtrude","SWEPT_BODY",BODY,{"disambiguationData":[OSD([sQuery(id+"F18.wireOp",EDGE,"E24"),sQuery(id+"F18.wireOp",EDGE,"E25"),sQuery(id+"F18.wireOp",EDGE,"E26"),sQuery(id+"F18.wireOp",EDGE,"E27")])]});
            var Q7;
            Q7=makeQuery(id+"F60.opRevolve","SWEPT_BODY",BODY,{"disambiguationData":[OSD([sQuery(id+"F59.wireOp",EDGE,"E64")])]});
            var Q8;
            Q8=makeQuery(id+"F80.opRevolve","SWEPT_BODY",BODY,{"disambiguationData":[OSD([sQuery(id+"F79.wireOp",EDGE,"E82")])]});
            var Q9;
            Q9=makeQuery(id+"F82.opRevolve","SWEPT_BODY",BODY,{"disambiguationData":[OSD([sQuery(id+"F81.wireOp",EDGE,"E84")])]});
            var Q10;
            Q10=makeQuery(id+"F86.opRevolve","SWEPT_BODY",BODY,{"disambiguationData":[OSD([sQuery(id+"F85.wireOp",EDGE,"E88")])]});
            var Q11;
            Q11=makeQuery(id+"F84.opRevolve","SWEPT_BODY",BODY,{"disambiguationData":[OSD([sQuery(id+"F83.wireOp",EDGE,"E86")])]});
            var Q12;
            Q12=qCreatedBy(makeId("Right.planeOp"),FACE);
            mirror(context, id + "F118", {"entities" : qUnion([Q0, Q1, Q2, Q3, Q4, Q5, Q6, Q7, Q8, Q9, Q10, Q11]), "mirrorPlane" : qUnion([Q12])});
        }
        {
            var Q0;
            Q0=makeQuery(id+"F33.opRevolve","SWEPT_BODY",BODY,{"disambiguationData":[OSD([sQuery(id+"F32.wireOp",EDGE,"E38")])]});
            var Q1;
            Q1=qCreatedBy(makeId("Right.planeOp"),FACE);
            mirror(context, id + "F119", {"entities" : qUnion([Q0]), "mirrorPlane" : qUnion([Q1])});
        }
    });
